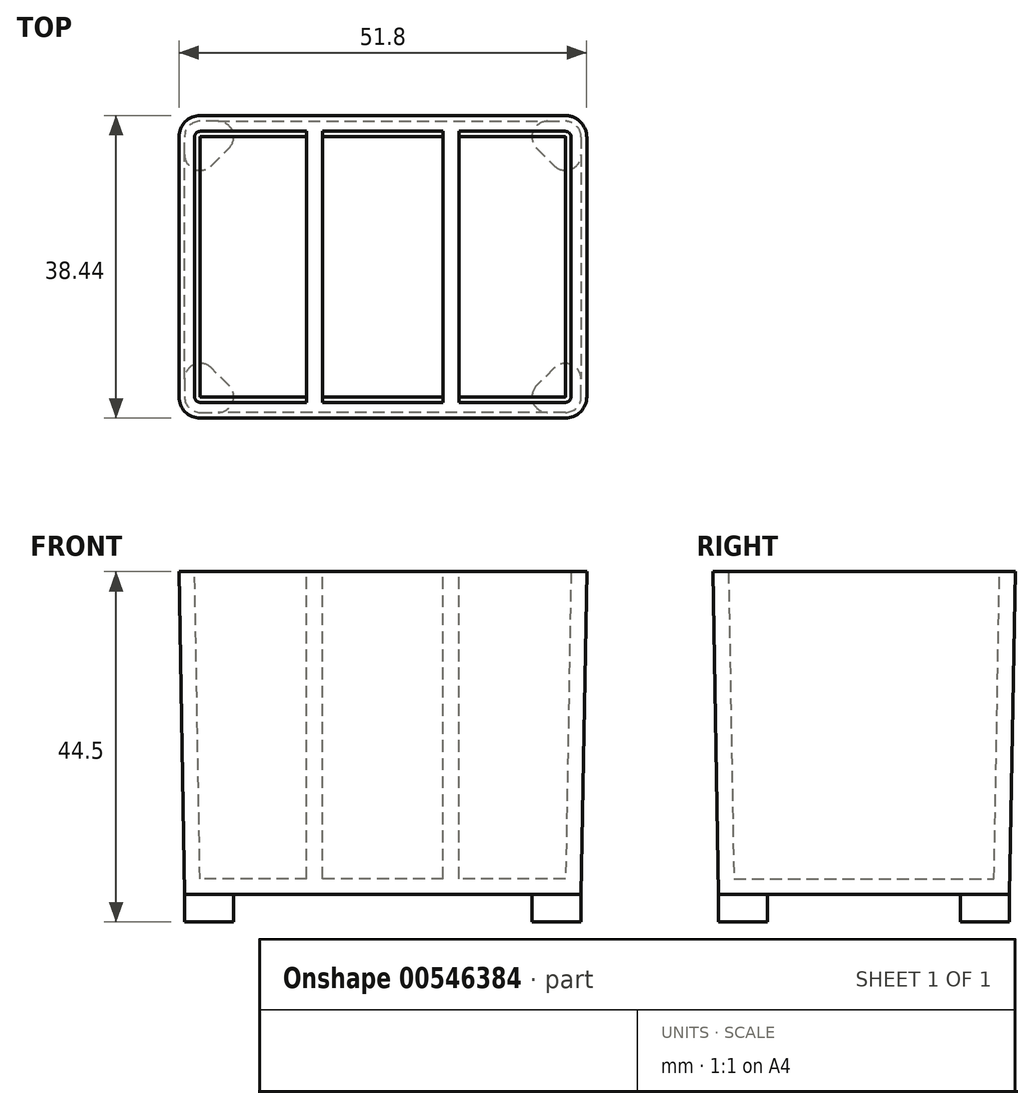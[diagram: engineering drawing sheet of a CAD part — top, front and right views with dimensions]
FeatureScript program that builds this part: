
annotation { "Feature Type Name" : "Feature", "Feature Type Description" : "" }
export const myFeature = defineFeature(function(context is Context, id is Id, definition is map)
    precondition{}
    {
        {
            var Q0;
            Q0=qCreatedBy(makeId("Top.planeOp"),FACE);
            var sketch = newSketch(context, id + "F0", { "sketchPlane" : qUnion([Q0])});
            skLineSegment(sketch, "E0.bottom", {"start": v(-20.94, 18.5) * mm, "end": v(-23.19, 18.5) * mm});
            skLineSegment(sketch, "E0.left", {"start": v(25.19, 16.5) * mm, "end": v(25.19, 14.26) * mm});
            skLineSegment(sketch, "E0.right", {"start": v(-25.19, -14.26) * mm, "end": v(-25.19, -16.5) * mm});
            skPoint(sketch, "E0.middle", {"position": v(0, 0) * mm});
            skPoint(sketch, "E1.visualSharp", {"position": v(-25.19, 18.5) * mm});
            skArc(sketch, "E1.filletArc", {"start": v(-23.19, 18.5) * mm, "mid": v(-24.6, 17.91) * mm, "end": v(-25.19, 16.5) * mm});
            skPoint(sketch, "E2.visualSharp", {"position": v(25.19, 18.5) * mm});
            skArc(sketch, "E2.filletArc", {"start": v(25.19, 16.5) * mm, "mid": v(24.6, 17.91) * mm, "end": v(23.19, 18.5) * mm});
            skPoint(sketch, "E3.visualSharp", {"position": v(25.19, -18.5) * mm});
            skArc(sketch, "E3.filletArc", {"start": v(23.19, -18.5) * mm, "mid": v(24.6, -17.91) * mm, "end": v(25.19, -16.5) * mm});
            skPoint(sketch, "E4.visualSharp", {"position": v(-25.19, -18.5) * mm});
            skLineSegment(sketch, "E5.0", {"start": v(-19.53, -15.09) * mm, "end": v(-21.77, -12.84) * mm});
            skLineSegment(sketch, "E6.0", {"start": v(-21.77, 12.84) * mm, "end": v(-19.53, 15.09) * mm});
            skLineSegment(sketch, "E7.0", {"start": v(21.77, -12.84) * mm, "end": v(19.53, -15.09) * mm});
            skLineSegment(sketch, "E8.0", {"start": v(19.53, 15.09) * mm, "end": v(21.77, 12.84) * mm});
            skPoint(sketch, "E9", {"position": v(-25.19, -9.43) * mm});
            skArc(sketch, "E10.filletArc", {"start": v(-21.77, -12.84) * mm, "mid": v(-23.95, -12.4) * mm, "end": v(-25.19, -14.26) * mm});
            skArc(sketch, "E11.filletArc", {"start": v(-20.94, -18.5) * mm, "mid": v(-19.1, -17.27) * mm, "end": v(-19.53, -15.09) * mm});
            skArc(sketch, "E12.filletArc", {"start": v(-19.53, 15.09) * mm, "mid": v(-19.1, 17.27) * mm, "end": v(-20.94, 18.5) * mm});
            skArc(sketch, "E13.filletArc", {"start": v(21.77, 12.84) * mm, "mid": v(23.95, 12.4) * mm, "end": v(25.19, 14.26) * mm});
            skLineSegment(sketch, "E14", {"start": v(20.94, 18.5) * mm, "end": v(23.19, 18.5) * mm});
            skLineSegment(sketch, "E15", {"start": v(25.19, -16.5) * mm, "end": v(25.19, -14.26) * mm});
            skLineSegment(sketch, "E16", {"start": v(23.19, -18.5) * mm, "end": v(20.94, -18.5) * mm});
            skLineSegment(sketch, "E17", {"start": v(-25.19, 14.26) * mm, "end": v(-25.19, 16.5) * mm});
            skArc(sketch, "E18.filletArc", {"start": v(-25.19, 14.26) * mm, "mid": v(-23.95, 12.4) * mm, "end": v(-21.77, 12.84) * mm});
            skArc(sketch, "E19.filletArc", {"start": v(19.53, -15.09) * mm, "mid": v(19.1, -17.27) * mm, "end": v(20.94, -18.5) * mm});
            skArc(sketch, "E20.filletArc", {"start": v(25.19, -14.26) * mm, "mid": v(23.95, -12.4) * mm, "end": v(21.77, -12.84) * mm});
            skArc(sketch, "E21.filletArc", {"start": v(20.94, 18.5) * mm, "mid": v(19.1, 17.27) * mm, "end": v(19.53, 15.09) * mm});
            skLineSegment(sketch, "E22", {"start": v(-20.94, 18.5) * mm, "end": v(20.94, 18.5) * mm});
            skLineSegment(sketch, "E23", {"start": v(25.19, 14.26) * mm, "end": v(25.19, -14.26) * mm});
            skLineSegment(sketch, "E24", {"start": v(20.94, -18.5) * mm, "end": v(-20.94, -18.5) * mm});
            skLineSegment(sketch, "E25", {"start": v(-25.19, 14.26) * mm, "end": v(-25.19, -14.26) * mm});
            skLineSegment(sketch, "E26", {"start": v(-23.19, -18.5) * mm, "end": v(-20.94, -18.5) * mm});
            skLineSegment(sketch, "E27", {"start": v(-23.19, -18.5) * mm, "end": v(-23.19, -18.5) * mm});
            skArc(sketch, "E28.filletArc", {"start": v(-25.19, -16.5) * mm, "mid": v(-24.6, -17.91) * mm, "end": v(-23.19, -18.5) * mm});
            skPoint(sketch, "E29.orphan", {"position": v(0, 18.5) * mm});
            skPoint(sketch, "E30.orphan", {"position": v(0, -18.5) * mm});
            skLineSegment(sketch, "E31.0", {"start": v(-9.67, 18.5) * mm, "end": v(-9.67, 1) * mm});
            skLineSegment(sketch, "E32.0", {"start": v(-7.67, 18.5) * mm, "end": v(-7.67, 1) * mm});
            skLineSegment(sketch, "E33.0", {"start": v(7.67, 18.5) * mm, "end": v(7.67, 1) * mm});
            skLineSegment(sketch, "E34.0", {"start": v(9.67, 18.5) * mm, "end": v(9.67, 1) * mm});
            skPoint(sketch, "E35.orphan", {"position": v(25.19, 0) * mm});
            skLineSegment(sketch, "E36.trimOffspring", {"start": v(7.67, -1) * mm, "end": v(7.67, -18.5) * mm});
            skLineSegment(sketch, "E37.trimOffspring", {"start": v(-7.67, -1) * mm, "end": v(-7.67, -18.5) * mm});
            skLineSegment(sketch, "E38.trimOffspring", {"start": v(-9.67, -1) * mm, "end": v(-9.67, -18.5) * mm});
            skPoint(sketch, "E39.start.orphan", {"position": v(-25.19, 0) * mm});
            skLineSegment(sketch, "E40.trimOffspring", {"start": v(9.67, -1) * mm, "end": v(9.67, -18.5) * mm});
            skLineSegment(sketch, "E41", {"start": v(-9.67, -1) * mm, "end": v(-9.67, 1) * mm});
            skLineSegment(sketch, "E42", {"start": v(-7.67, -1) * mm, "end": v(-7.67, 1) * mm});
            skLineSegment(sketch, "E43", {"start": v(7.67, -1) * mm, "end": v(7.67, 1) * mm});
            skLineSegment(sketch, "E44", {"start": v(9.67, 1) * mm, "end": v(9.67, -1) * mm});
            skSolve(sketch);
        }
        {
            var Q0;
            Q0=makeQuery(id+"F0.imprint","IMPRINT",FACE,{"disambiguationData":[TD([[makeQuery(id+"F0.imprint","IMPRINT",EDGE,{"derivedFrom":sQuery(id+"F0.wireOp",EDGE,"E0.bottom")}),1.0]])]});
            var Q1;
            Q1=makeQuery(id+"F0.imprint","IMPRINT",FACE,{"disambiguationData":[TD([[makeQuery(id+"F0.imprint","IMPRINT",EDGE,{"derivedFrom":sQuery(id+"F0.wireOp",EDGE,"E0.left")}),-1.0]])]});
            var Q2;
            Q2=makeQuery(id+"F0.imprint","IMPRINT",FACE,{"disambiguationData":[TD([[makeQuery(id+"F0.imprint","IMPRINT",EDGE,{"derivedFrom":sQuery(id+"F0.wireOp",EDGE,"E3.filletArc")}),1.0]])]});
            var Q3;
            Q3=makeQuery(id+"F0.imprint","IMPRINT",FACE,{"disambiguationData":[TD([[makeQuery(id+"F0.imprint","IMPRINT",EDGE,{"derivedFrom":sQuery(id+"F0.wireOp",EDGE,"E0.right")}),1.0]])]});
            extrude(context, id + "F1", {"entities" : qUnion([Q0, Q1, Q2, Q3]), "oppositeDirection" : true, "depth" : 3.5 * mm, "offsetDistance" : 25 * mm});
        }
        {
            var Q0;
            Q0=qSketchRegion(id+"F0",true);
            var Q1;
            Q1=makeQuery(id+"F1.opExtrude","CAP_FACE",FACE,{"disambiguationData":[OSD([sQuery(id+"F0.wireOp",EDGE,"E0.right"),sQuery(id+"F0.wireOp",EDGE,"E5.0"),sQuery(id+"F0.wireOp",EDGE,"E10.filletArc"),sQuery(id+"F0.wireOp",EDGE,"E11.filletArc"),sQuery(id+"F0.wireOp",EDGE,"E26"),sQuery(id+"F0.wireOp",EDGE,"E28.filletArc")])],"isStart":true});
            extrude(context, id + "F2", {"entities" : qUnion([Q0, Q1]), "operationType" : NewBodyOperationType.ADD, "depth" : 41 * mm, "offsetDistance" : 25 * mm, "hasDraft" : true, "draftAngle" : 1 * degree});
        }
        {
            var Q0;
            Q0=makeQuery(id+"F2.opExtrude","CAP_FACE",FACE,{"disambiguationData":[OSD([sQuery(id+"F0.wireOp",EDGE,"E0.bottom"),sQuery(id+"F0.wireOp",EDGE,"E0.left"),sQuery(id+"F0.wireOp",EDGE,"E0.right"),sQuery(id+"F0.wireOp",EDGE,"E1.filletArc"),sQuery(id+"F0.wireOp",EDGE,"E2.filletArc"),sQuery(id+"F0.wireOp",EDGE,"E3.filletArc"),sQuery(id+"F0.wireOp",EDGE,"E14"),sQuery(id+"F0.wireOp",EDGE,"E15"),sQuery(id+"F0.wireOp",EDGE,"E16"),sQuery(id+"F0.wireOp",EDGE,"E17"),sQuery(id+"F0.wireOp",EDGE,"E22"),sQuery(id+"F0.wireOp",EDGE,"E23"),sQuery(id+"F0.wireOp",EDGE,"E24"),sQuery(id+"F0.wireOp",EDGE,"E25"),sQuery(id+"F0.wireOp",EDGE,"E26"),sQuery(id+"F0.wireOp",EDGE,"E28.filletArc")])],"isStart":false});
            shell(context, id + "F3", {"entities" : qUnion([Q0]), "thickness" : 2 * mm});
        }
        {
            var Q0;
            {var subQ0=sQuery(id+"F0.wireOp",EDGE,"E33.0");Q0=makeQuery(id+"F0.imprint","IMPRINT",FACE,{"disambiguationData":[TD([[makeQuery(id+"F0.imprint","IMPRINT",EDGE,{"derivedFrom":subQ0}),1.0]])]});}
            var Q1;
            {var subQ1=sQuery(id+"F0.wireOp",EDGE,"E31.0");Q1=makeQuery(id+"F0.imprint","IMPRINT",FACE,{"disambiguationData":[TD([[makeQuery(id+"F0.imprint","IMPRINT",EDGE,{"derivedFrom":subQ1}),1.0]])]});}
            var Q2;
            Q2=sQuery(id+"F0.wireOp",EDGE,"E38.trimOffspring");
            extrude(context, id + "F4", {"entities" : qUnion([Q0, Q1]), "operationType" : NewBodyOperationType.ADD, "surfaceEntities" : qUnion([Q2]), "depth" : 41 * mm, "offsetDistance" : 25 * mm});
        }
        {
            var Q0;
            Q0=makeQuery(id+"F0.imprint","IMPRINT",FACE,{"disambiguationData":[TD([[makeQuery(id+"F0.imprint","IMPRINT",EDGE,{"derivedFrom":sQuery(id+"F0.wireOp",EDGE,"E0.bottom")}),1.0]])]});
            var Q1;
            Q1=makeQuery(id+"F0.imprint","IMPRINT",FACE,{"disambiguationData":[TD([[makeQuery(id+"F0.imprint","IMPRINT",EDGE,{"derivedFrom":sQuery(id+"F0.wireOp",EDGE,"E3.filletArc")}),1.0]])]});
            var Q2;
            Q2=makeQuery(id+"F0.imprint","IMPRINT",FACE,{"disambiguationData":[TD([[makeQuery(id+"F0.imprint","IMPRINT",EDGE,{"derivedFrom":sQuery(id+"F0.wireOp",EDGE,"E0.left")}),-1.0]])]});
            var Q3;
            Q3=makeQuery(id+"F0.imprint","IMPRINT",FACE,{"disambiguationData":[TD([[makeQuery(id+"F0.imprint","IMPRINT",EDGE,{"derivedFrom":sQuery(id+"F0.wireOp",EDGE,"E0.right")}),1.0]])]});
            extrude(context, id + "F5", {"entities" : qUnion([Q0, Q1, Q2, Q3]), "operationType" : NewBodyOperationType.ADD, "oppositeDirection" : true, "depth" : 2 * mm, "offsetDistance" : 25 * mm, "hasSecondDirection" : true, "secondDirectionOppositeDirection" : false, "secondDirectionDepth" : 2 * mm});
        }
    });
